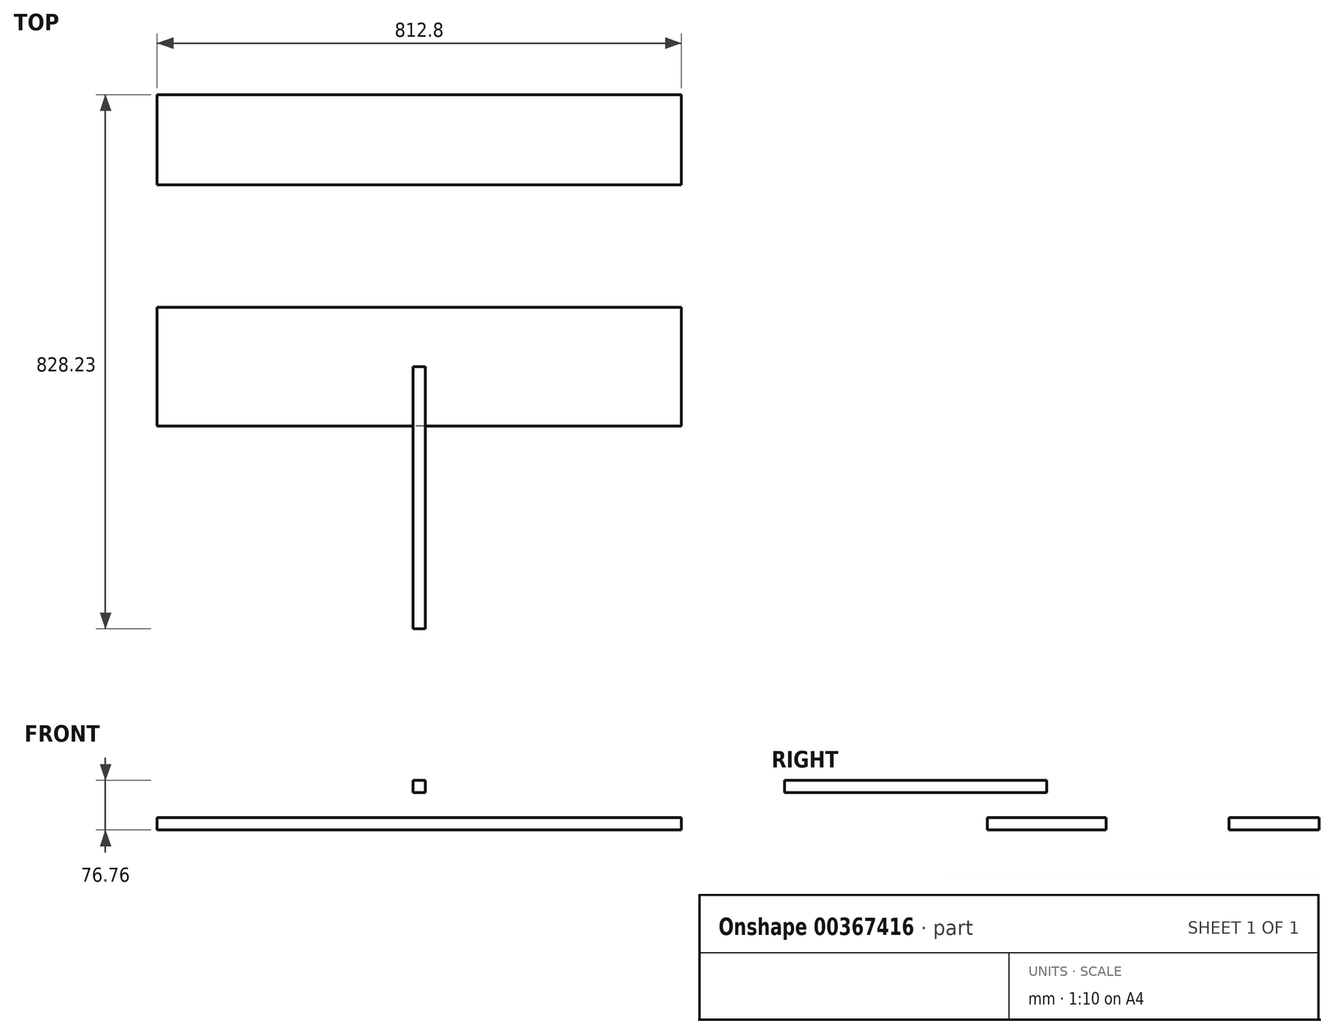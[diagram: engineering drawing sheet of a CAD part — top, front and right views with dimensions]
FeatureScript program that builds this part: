
annotation { "Feature Type Name" : "Feature", "Feature Type Description" : "" }
export const myFeature = defineFeature(function(context is Context, id is Id, definition is map)
    precondition{}
    {
        {
            var Q0;
            Q0=qCreatedBy(makeId("Top.planeOp"),FACE);
            var sketch = newSketch(context, id + "F0", { "sketchPlane" : qUnion([Q0])});
            skLineSegment(sketch, "E0.bottom", {"start": v(406.4, 92.08) * mm, "end": v(-406.4, 92.08) * mm});
            skLineSegment(sketch, "E0.top", {"start": v(406.4, -92.08) * mm, "end": v(-406.4, -92.08) * mm});
            skLineSegment(sketch, "E0.left", {"start": v(406.4, 92.08) * mm, "end": v(406.4, -92.08) * mm});
            skLineSegment(sketch, "E0.right", {"start": v(-406.4, 92.08) * mm, "end": v(-406.4, -92.08) * mm});
            skPoint(sketch, "E0.middle", {"position": v(0, 0) * mm});
            skSolve(sketch);
        }
        {
            var Q0;
            Q0=makeQuery(id+"F0.imprint","IMPRINT",FACE,{"disambiguationData":[TD([[makeQuery(id+"F0.imprint","IMPRINT",EDGE,{"derivedFrom":sQuery(id+"F0.wireOp",EDGE,"E0.bottom")}),1.0]])]});
            extrude(context, id + "F1", {"entities" : qUnion([Q0]), "depth" : 19.05 * mm});
        }
        {
            var Q0;
            Q0=qCreatedBy(makeId("Front.planeOp"),FACE);
            var sketch = newSketch(context, id + "F2", { "sketchPlane" : qUnion([Q0])});
            skLineSegment(sketch, "E1.bottom", {"start": v(9.52, 76.76) * mm, "end": v(-9.53, 76.76) * mm});
            skLineSegment(sketch, "E1.top", {"start": v(9.52, 57.71) * mm, "end": v(-9.53, 57.71) * mm});
            skLineSegment(sketch, "E1.left", {"start": v(9.52, 76.76) * mm, "end": v(9.52, 57.71) * mm});
            skLineSegment(sketch, "E1.right", {"start": v(-9.53, 76.76) * mm, "end": v(-9.53, 57.71) * mm});
            skPoint(sketch, "E1.middle", {"position": v(0, 67.24) * mm});
            skSolve(sketch);
        }
        {
            var Q0;
            Q0 = qSketchRegion(id + "F2", true);
            extrude(context, id + "F3", {"entities" : qUnion([Q0]), "depth" : 406.4 * mm});
        }
        {
            var Q0;
            Q0=qCreatedBy(makeId("Top.planeOp"),FACE);
            var sketch = newSketch(context, id + "F4", { "sketchPlane" : qUnion([Q0])});
            skLineSegment(sketch, "E2.bottom", {"start": v(406.4, 421.83) * mm, "end": v(-406.4, 421.83) * mm});
            skLineSegment(sketch, "E2.top", {"start": v(406.4, 282.13) * mm, "end": v(-406.4, 282.13) * mm});
            skLineSegment(sketch, "E2.left", {"start": v(406.4, 421.83) * mm, "end": v(406.4, 282.13) * mm});
            skLineSegment(sketch, "E2.right", {"start": v(-406.4, 421.83) * mm, "end": v(-406.4, 282.13) * mm});
            skPoint(sketch, "E2.middle", {"position": v(0, 351.98) * mm});
            skSolve(sketch);
        }
        {
            var Q0;
            Q0 = qSketchRegion(id + "F4", true);
            extrude(context, id + "F5", {"entities" : qUnion([Q0]), "depth" : 19.05 * mm});
        }
    });
